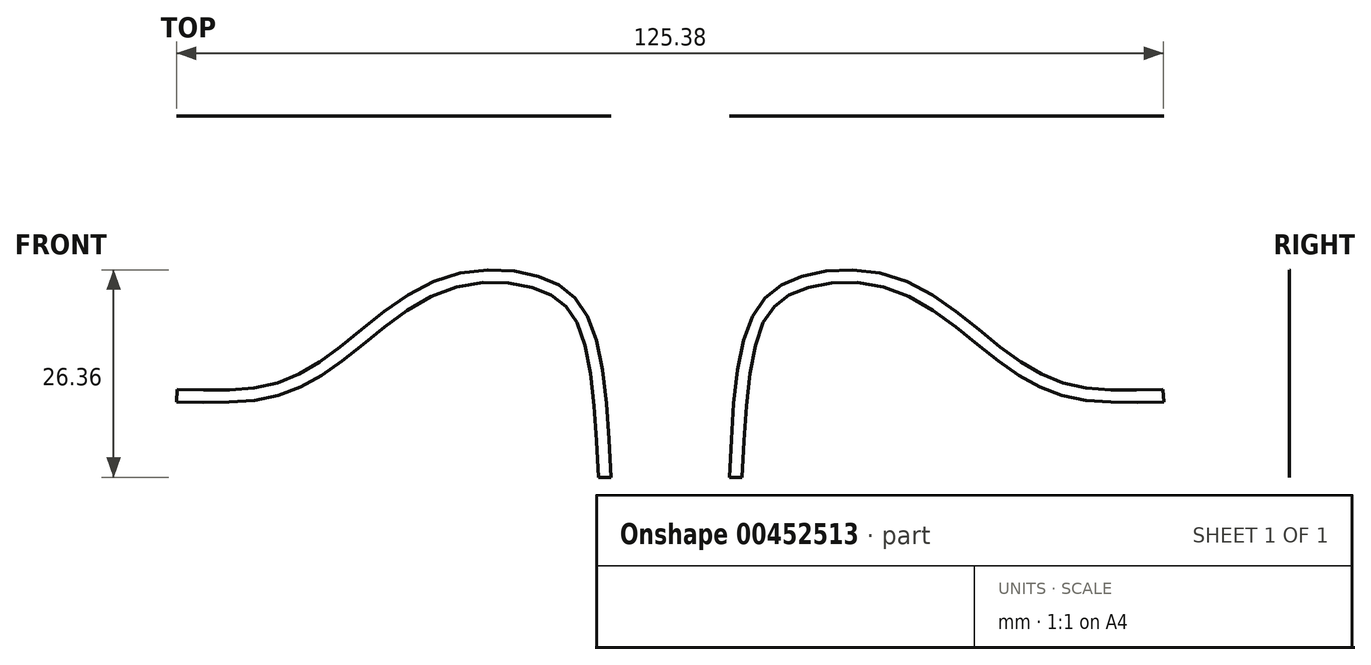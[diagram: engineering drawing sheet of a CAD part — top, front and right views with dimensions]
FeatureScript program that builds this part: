
annotation { "Feature Type Name" : "Feature", "Feature Type Description" : "" }
export const myFeature = defineFeature(function(context is Context, id is Id, definition is map)
    precondition{}
    {
        {
            var Q0;
            Q0=qCreatedBy(makeId("Front.planeOp"),FACE);
            var sketch = newSketch(context, id + "F0", { "sketchPlane" : qUnion([Q0])});
            skFitSpline(sketch, "E0", {"points": [v(-7.53, 0) * mm, v(-10.21, 19.89) * mm, v(-16.34, 25.39) * mm, v(-28.98, 25.27) * mm, v(-41.42, 16.97) * mm, v(-50.81, 11.73) * mm, v(-62.6, 11.15) * mm], "startDerivative": vector(-5.22, 111.22) * mm, "endDerivative": vector(-77.4, 0.94) * mm});
            skFitSpline(sketch, "E1.MirrorCS", {"points": [v(7.53, 0) * mm, v(10.21, 19.89) * mm, v(16.34, 25.39) * mm, v(28.98, 25.27) * mm, v(41.42, 16.97) * mm, v(50.81, 11.73) * mm, v(62.6, 11.15) * mm], "startDerivative": vector(5.22, 111.22) * mm, "endDerivative": vector(77.4, 0.94) * mm});
            skFitSpline(sketch, "E2", {"points": [v(-9.11, 0) * mm, v(-11.55, 19.03) * mm, v(-16.62, 23.83) * mm, v(-28.28, 23.84) * mm, v(-40.38, 15.78) * mm, v(-50.25, 10.25) * mm, v(-62.7, 9.57) * mm], "startDerivative": vector(-6.04, 107.2) * mm, "endDerivative": vector(-76.86, 0.23) * mm});
            skLineSegment(sketch, "E3", {"start": v(-62.6, 11.15) * mm, "end": v(-62.7, 9.57) * mm});
            skLineSegment(sketch, "E4", {"start": v(-9.11, 0) * mm, "end": v(-7.53, 0) * mm});
            skLineSegment(sketch, "E5.MirrorCS", {"start": v(62.6, 11.15) * mm, "end": v(62.7, 9.57) * mm});
            skLineSegment(sketch, "E6.MirrorCS", {"start": v(9.11, 0) * mm, "end": v(7.53, 0) * mm});
            skFitSpline(sketch, "E7.MirrorCS", {"points": [v(9.11, 0) * mm, v(11.55, 19.03) * mm, v(16.62, 23.83) * mm, v(28.28, 23.84) * mm, v(40.38, 15.78) * mm, v(50.25, 10.25) * mm, v(62.7, 9.57) * mm], "startDerivative": vector(6.04, 107.2) * mm, "endDerivative": vector(76.86, 0.23) * mm});
            skSolve(sketch);
        }
        {
            var Q0;
            Q0 = qSketchRegion(id + "F0", true);
            extrude(context, id + "F1", {"entities" : qUnion([Q0]), "depth" : 1 / 406.4 * mm, "offsetDistance" : 25.4 * mm});
        }
    });
